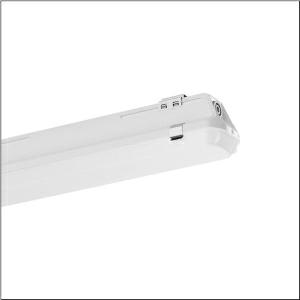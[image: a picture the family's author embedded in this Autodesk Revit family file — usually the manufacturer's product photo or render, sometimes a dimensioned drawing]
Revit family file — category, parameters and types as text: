
# Revit family: monsun_r__11_51fp20tp960x_3aeb
name_source: partatom
category: Lighting Fixtures
units: mm (PartAtom-declared; Revit-internal decimal feet)

## family parameters
Cut with Voids When Loaded = No
Host = Face
Light Source = No
Part Type = Normal
Room Calculation Point = No
Round Connector Dimension = Use Diameter
Shared = No

## types (1)
- --- (1 x LED 2700 K ... 6500 K, 5420 lm, 36.8 W, 6500K)
    Apparent Load = 37 VA
    CIE Flux Codes = 45 75 93 94 100
    Color Rendering = 80
    Color Temperature = 6500K
    Default Elevation = 1800 mm
    Description = Monsun® 11, damp-proof luminaire, chain hanger, primary optical cover: enclosure, of PC, light emission: direct distribution, primary light characteristic: symmetric, installation type: suspended mounting, surface-mounted, horizontal mounting, vertical mounting, LED, rated luminous flux: 5.410lm, luminous efficacy: 147lm/W, light colour: 8tw, colour temperature: 2700..6500K, control gear: ECG DALI, with terminal, 5-pole, max. 2.5mm², mains connection: 220..240V, AC, 50/60Hz, rated input power: 37W, luminaire housing, of glass-fibre reinforced polyester, uncoated, bright grey, incl. chain hanger, length: 1.590mm, width: 90mm, height: 88mm, clip for enclosure, of stainless steel (V2A), ceiling mounting element, of stainless steel (V2A), chain hanger, of stainless steel (V2A), protection rating (complete): IP66, insulation class (complete): insulation class I (protective earthing), certification: CE, ENEC, VDE, UKCA, protection symbol: D, impact resistance: IK08, permissible operating ambient temperature: -25..+35°C, standard: EN 50419, EN 60598-2-1, no direct snow, no direct sun, no direct rain, for indoor or canopied outdoor use, corresponds to IFS (International Featured Standards) requirements for safety and quality in the food industry, contact your sales advisor before using the luminaires in applications with unclear chemical exposure, large temperature fluctuations or condensation-forming humidity, LABS conformity tested according to VDMA 24364:2018-05, packaging unit: 1 piece
    Height = 89 mm
    Lamp = 1 x LED 2700 K ... 6500 K
    Lamp Light Flux = 5420 lm
    Lamp Power = 36.8 W
    Lamp count = 1
    Length = 1590 mm
    Luminous efficacy = 147 lm/W
    Manufacturer = Siteco
    ModVariant = No
    Model = 51FP20TP960X
    Mounting Place = Ceiling
    Mounting Type = Surface mounted
    Number of Poles = 1
    OnlyDefault = Yes
    Power Factor = 1
    Product Name = Monsun® 11
    Product group = damp-proof luminaire
    ProductGroupID = 300
    Protection Class = Protection class I
    Protection Degree = IP 66
    RLX_Detail_Level = 1
    RLX_Emergency_Light_Flux = 0 lm
    RLX_Emergency_Type = 0
    RLX_Emergency_Type_DB = No
    RlxData = <blob elided: 89225 chars, md5=440a5580>
    Socket = socket
    Standby Power = 0 W
    System Light Flux = 5420 lm
    System Power = 37 W
    Type Comments = individual setting: CCT=6500K
    Type Image = l_1004748.jpg
    URL = http://relux.com
    VarID = @adj_140519
    Voltage = 0 V
    Weight = 0.00 kg
    Width = 90 mm

## geometry (parser evidence)
native form markers: Blend x4, Sweep x14
no freeform markers — native parametric forms only
